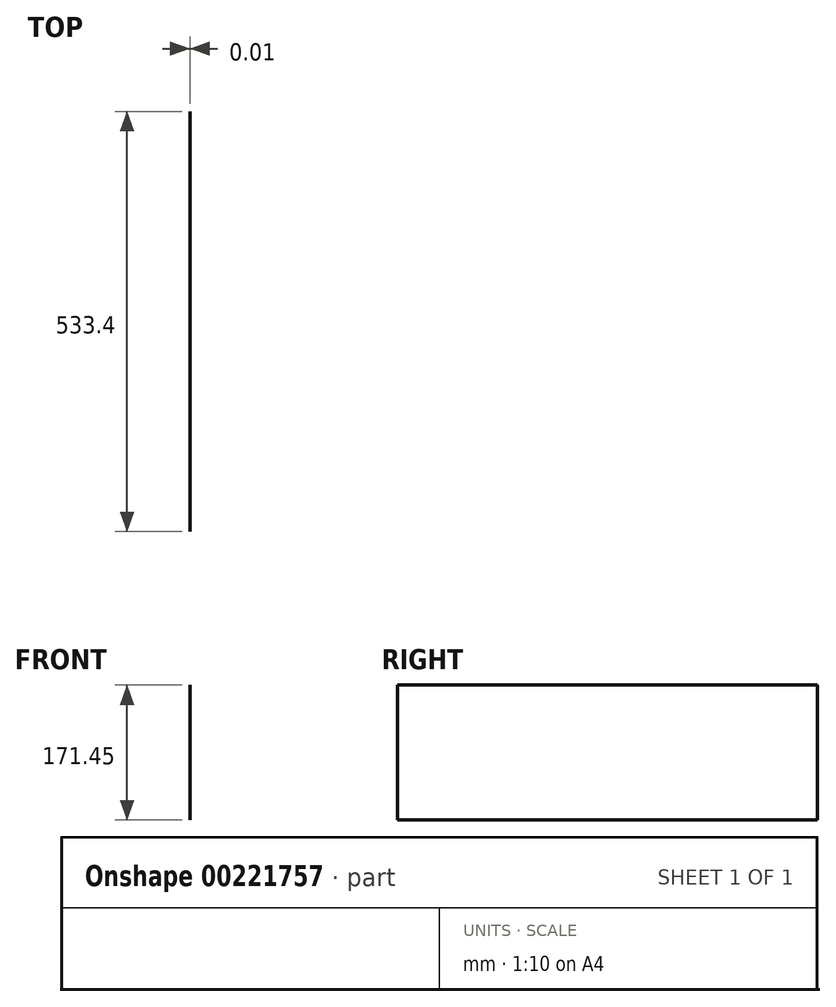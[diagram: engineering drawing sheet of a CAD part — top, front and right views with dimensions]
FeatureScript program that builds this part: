
annotation { "Feature Type Name" : "Feature", "Feature Type Description" : "" }
export const myFeature = defineFeature(function(context is Context, id is Id, definition is map)
    precondition{}
    {
        {
            var Q0;
            Q0=qCreatedBy(makeId("Right.planeOp"),FACE);
            var sketch = newSketch(context, id + "F0", { "sketchPlane" : qUnion([Q0])});
            skLineSegment(sketch, "E0.bottom", {"start": v(-327.57, -67.2) * mm, "end": v(205.83, -67.2) * mm});
            skLineSegment(sketch, "E0.top", {"start": v(-327.57, 104.26) * mm, "end": v(205.83, 104.26) * mm});
            skLineSegment(sketch, "E0.left", {"start": v(-327.57, -67.2) * mm, "end": v(-327.57, 104.26) * mm});
            skLineSegment(sketch, "E0.right", {"start": v(205.83, -67.2) * mm, "end": v(205.83, 104.26) * mm});
            skSolve(sketch);
        }
        {
            var Q0;
            Q0=makeQuery(id+"F0.imprint","IMPRINT",FACE,{"disambiguationData":[TD([[makeQuery(id+"F0.imprint","IMPRINT",EDGE,{"derivedFrom":sQuery(id+"F0.wireOp",EDGE,"E0.bottom")}),1.0]])]});
            extrude(context, id + "F1", {"entities" : qUnion([Q0]), "oppositeDirection" : true, "depth" : 3 / 406.4 * mm});
        }
    });
